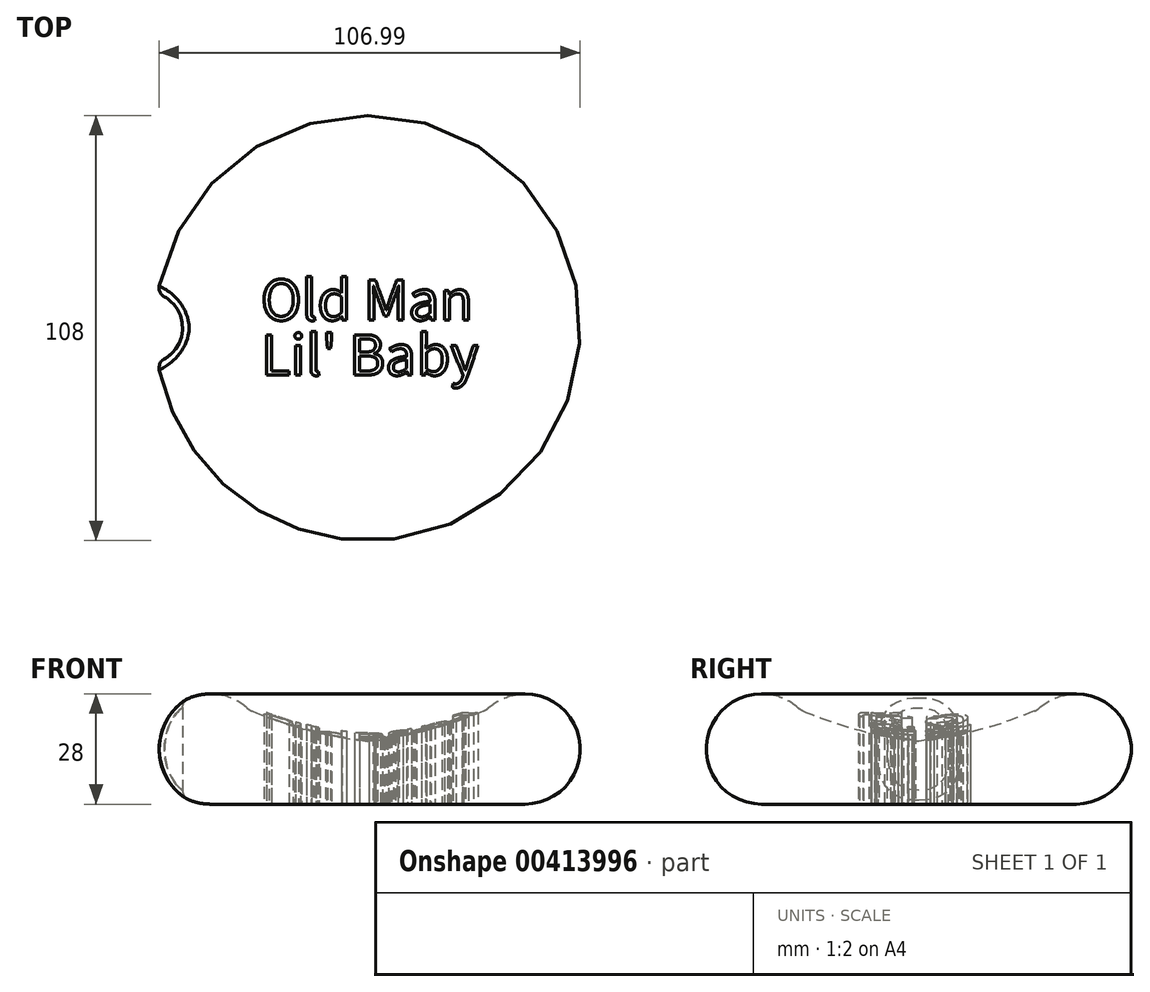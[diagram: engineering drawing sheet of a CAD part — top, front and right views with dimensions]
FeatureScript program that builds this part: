
annotation { "Feature Type Name" : "Feature", "Feature Type Description" : "" }
export const myFeature = defineFeature(function(context is Context, id is Id, definition is map)
    precondition{}
    {
        {
            var Q0;
            Q0=qCreatedBy(makeId("Right.planeOp"),FACE);
            var sketch = newSketch(context, id + "F0", { "sketchPlane" : qUnion([Q0])});
            skArc(sketch, "E0", {"start": v(-29.4, 23.66) * mm, "mid": v(-14.98, 18.77) * mm, "end": v(0, 16) * mm});
            skArc(sketch, "E1", {"start": v(-30.76, 24.52) * mm, "mid": v(-53.1, 18.94) * mm, "end": v(-40, 0) * mm});
            skPoint(sketch, "E2", {"position": v(-30.21, 24.01) * mm});
            skLineSegment(sketch, "E3", {"start": v(-40, 0) * mm, "end": v(0, 0) * mm});
            skLineSegment(sketch, "E4", {"start": v(0, 0) * mm, "end": v(0, 16) * mm});
            skArc(sketch, "E5.filletArc", {"start": v(-30.76, 24.52) * mm, "mid": v(-30.11, 24.04) * mm, "end": v(-29.4, 23.66) * mm});
            skSolve(sketch);
        }
        {
            var Q0;
            Q0=makeQuery(id+"F0.imprint","IMPRINT",FACE,{"disambiguationData":[TD([[makeQuery(id+"F0.imprint","IMPRINT",EDGE,{"derivedFrom":sQuery(id+"F0.wireOp",EDGE,"E0")}),-1.0]])]});
            var Q1;
            Q1=sQuery(id+"F0.wireOp",EDGE,"E4");
            revolve(context, id + "F1", {"entities" : qUnion([Q0]), "axis" : qUnion([Q1]), "revolveType" : RevolveType.FULL});
        }
        {
            var Q0;
            Q0=qCreatedBy(makeId("Top.planeOp"),FACE);
            var sketch = newSketch(context, id + "F2", { "sketchPlane" : qUnion([Q0])});
            skText(sketch, "E6", { "text": "Old Man\nLil\' Baby", "fontName": "NotoSansCJKsc-Regular.otf"});
            const initialGuessF2  = {"E6": [-0.02713, 0.00197, 1, 0, 0.01006]};
            skSetInitialGuess(sketch, initialGuessF2);
            skSolve(sketch);
        }
        {
            var Q0;
            Q0 = qSketchRegion(id + "F2", true);
            extrude(context, id + "F3", {"entities" : qUnion([Q0]), "operationType" : NewBodyOperationType.REMOVE, "endBound" : BoundingType.THROUGH_ALL, "depth" : 25 * mm});
        }
        {
            var Q0;
            Q0=qCreatedBy(makeId("Top.planeOp"),FACE);
            var sketch = newSketch(context, id + "F4", { "sketchPlane" : qUnion([Q0])});
            skCircle(sketch, "E7", {"center": v(-55.99, 0) * mm, "radius": 9 * mm});
            skSolve(sketch);
        }
        {
            var Q0;
            Q0=makeQuery(id+"F4.imprint","IMPRINT",FACE,{"disambiguationData":[TD([[makeQuery(id+"F4.imprint","IMPRINT",EDGE,{"derivedFrom":sQuery(id+"F4.wireOp",EDGE,"E7")}),1.0]])]});
            extrude(context, id + "F5", {"entities" : qUnion([Q0]), "operationType" : NewBodyOperationType.REMOVE, "endBound" : BoundingType.THROUGH_ALL, "depth" : 25 * mm});
        }
        {
            var Q0;
            Q0=makeQuery(id+"F1.opRevolve","SWEPT_FACE",FACE,{"disambiguationData":[OSD([sQuery(id+"F0.wireOp",EDGE,"E1")])]});
            fillet(context, id + "F6", {"entities" : qUnion([Q0]), "radius" : 2.6 * mm, "tangentPropagation" : true, "allowEdgeOverflow" : false});
        }
    });
